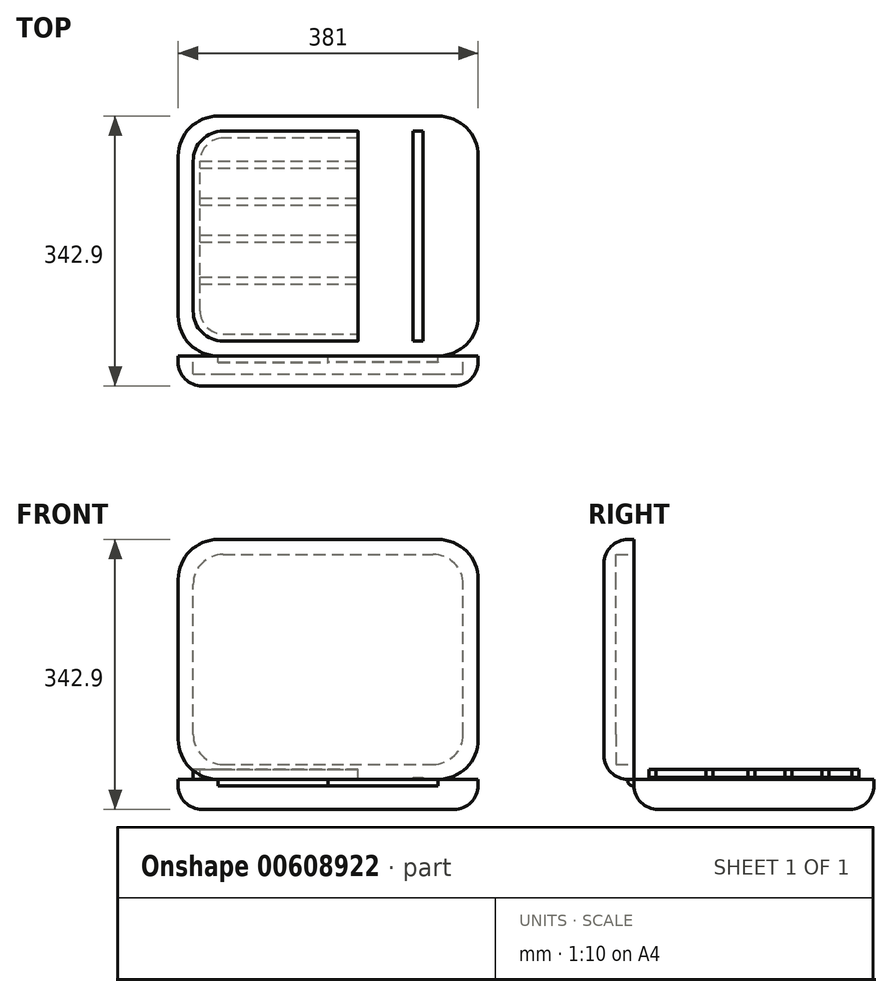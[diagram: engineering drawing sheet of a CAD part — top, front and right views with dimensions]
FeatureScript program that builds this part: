
annotation { "Feature Type Name" : "Feature", "Feature Type Description" : "" }
export const myFeature = defineFeature(function(context is Context, id is Id, definition is map)
    precondition{}
    {
        {
            var Q0;
            Q0=qCreatedBy(makeId("Top.planeOp"),FACE);
            var sketch = newSketch(context, id + "F0", { "sketchPlane" : qUnion([Q0])});
            skLineSegment(sketch, "E0.bottom", {"start": v(139.7, -152.4) * mm, "end": v(-139.7, -152.4) * mm});
            skLineSegment(sketch, "E0.top", {"start": v(139.7, 152.4) * mm, "end": v(-139.7, 152.4) * mm});
            skLineSegment(sketch, "E0.left", {"start": v(190.5, -101.6) * mm, "end": v(190.5, 101.6) * mm});
            skLineSegment(sketch, "E0.right", {"start": v(-190.5, -101.6) * mm, "end": v(-190.5, 101.6) * mm});
            skPoint(sketch, "E0.middle", {"position": v(0, 0) * mm});
            skPoint(sketch, "E1.visualSharp", {"position": v(-190.5, 152.4) * mm});
            skArc(sketch, "E1.filletArc", {"start": v(-139.7, 152.4) * mm, "mid": v(-175.62, 137.52) * mm, "end": v(-190.5, 101.6) * mm});
            skPoint(sketch, "E2.visualSharp", {"position": v(190.5, 152.4) * mm});
            skArc(sketch, "E2.filletArc", {"start": v(190.5, 101.6) * mm, "mid": v(175.62, 137.52) * mm, "end": v(139.7, 152.4) * mm});
            skPoint(sketch, "E3.visualSharp", {"position": v(190.5, -152.4) * mm});
            skArc(sketch, "E3.filletArc", {"start": v(139.7, -152.4) * mm, "mid": v(175.62, -137.52) * mm, "end": v(190.5, -101.6) * mm});
            skPoint(sketch, "E4.visualSharp", {"position": v(-190.5, -152.4) * mm});
            skArc(sketch, "E4.filletArc", {"start": v(-190.5, -101.6) * mm, "mid": v(-175.62, -137.52) * mm, "end": v(-139.7, -152.4) * mm});
            skSolve(sketch);
        }
        {
            var Q0;
            Q0=makeQuery(id+"F0.imprint","IMPRINT",FACE,{"disambiguationData":[TD([[makeQuery(id+"F0.imprint","IMPRINT",EDGE,{"derivedFrom":sQuery(id+"F0.wireOp",EDGE,"E0.bottom")}),-1.0]])]});
            extrude(context, id + "F1", {"entities" : qUnion([Q0]), "depth" : 38.1 * mm, "offsetDistance" : 25.4 * mm});
        }
        {
            var Q0;
            Q0=makeQuery(id+"F1.opExtrude","CAP_EDGE",EDGE,{"disambiguationData":[OSD([sQuery(id+"F0.wireOp",EDGE,"E0.bottom")])],"isStart":true});
            fillet(context, id + "F2", {"entities" : qUnion([Q0]), "radius" : 30.48 * mm, "tangentPropagation" : true, "allowEdgeOverflow" : false});
        }
        {
            var Q0;
            Q0=makeQuery(id+"F1.opExtrude","SWEPT_FACE",FACE,{"disambiguationData":[OSD([sQuery(id+"F0.wireOp",EDGE,"E0.bottom")])]});
            var sketch = newSketch(context, id + "F3", { "sketchPlane" : qUnion([Q0])});
            skLineSegment(sketch, "E5.bottom", {"start": v(-139.7, 342.9) * mm, "end": v(139.7, 342.9) * mm});
            skLineSegment(sketch, "E5.top", {"start": v(-139.7, 38.1) * mm, "end": v(139.7, 38.1) * mm});
            skLineSegment(sketch, "E5.left", {"start": v(-190.5, 292.1) * mm, "end": v(-190.5, 88.9) * mm});
            skLineSegment(sketch, "E5.right", {"start": v(190.5, 292.1) * mm, "end": v(190.5, 88.9) * mm});
            skPoint(sketch, "E6.visualSharp", {"position": v(-190.5, 342.9) * mm});
            skArc(sketch, "E6.filletArc", {"start": v(-139.7, 342.9) * mm, "mid": v(-175.62, 328.02) * mm, "end": v(-190.5, 292.1) * mm});
            skPoint(sketch, "E7.visualSharp", {"position": v(190.5, 342.9) * mm});
            skArc(sketch, "E7.filletArc", {"start": v(190.5, 292.1) * mm, "mid": v(175.62, 328.02) * mm, "end": v(139.7, 342.9) * mm});
            skPoint(sketch, "E8.visualSharp", {"position": v(190.5, 38.1) * mm});
            skArc(sketch, "E8.filletArc", {"start": v(139.7, 38.1) * mm, "mid": v(175.62, 52.98) * mm, "end": v(190.5, 88.9) * mm});
            skPoint(sketch, "E9.visualSharp", {"position": v(-190.5, 38.1) * mm});
            skArc(sketch, "E9.filletArc", {"start": v(-190.5, 88.9) * mm, "mid": v(-175.62, 52.98) * mm, "end": v(-139.7, 38.1) * mm});
            skSolve(sketch);
        }
        {
            var Q0;
            Q0 = qSketchRegion(id + "F3", true);
            extrude(context, id + "F4", {"entities" : qUnion([Q0]), "depth" : 38.1 * mm, "offsetDistance" : 25.4 * mm});
        }
        {
            var Q0;
            Q0=makeQuery(id+"F4.opExtrude","CAP_EDGE",EDGE,{"disambiguationData":[OSD([sQuery(id+"F3.wireOp",EDGE,"E5.left")])],"isStart":false});
            fillet(context, id + "F5", {"entities" : qUnion([Q0]), "radius" : 30.48 * mm, "tangentPropagation" : true, "allowEdgeOverflow" : false});
        }
        {
            var Q0;
            Q0=qCreatedBy(makeId("Right.planeOp"),FACE);
            var sketch = newSketch(context, id + "F6", { "sketchPlane" : qUnion([Q0])});
            skArc(sketch, "E10", {"start": v(-160.02, 38.1) * mm, "mid": v(-158.64, 31.86) * mm, "end": v(-152.4, 30.48) * mm});
            skLineSegment(sketch, "E11", {"start": v(-160.02, 38.1) * mm, "end": v(-152.4, 38.1) * mm});
            skLineSegment(sketch, "E12", {"start": v(-152.4, 38.1) * mm, "end": v(-152.4, 30.48) * mm});
            skSolve(sketch);
        }
        {
            var Q0;
            Q0 = qSketchRegion(id + "F6", true);
            extrude(context, id + "F7", {"entities" : qUnion([Q0]), "depth" : 139.7 * mm, "offsetDistance" : 25.4 * mm});
        }
        {
            var Q0;
            Q0=makeQuery(id+"F7.opExtrude","CAP_FACE",FACE,{"disambiguationData":[OSD([sQuery(id+"F6.wireOp",EDGE,"E10"),sQuery(id+"F6.wireOp",EDGE,"E11"),sQuery(id+"F6.wireOp",EDGE,"E12")])],"isStart":true});
            extrude(context, id + "F8", {"entities" : qUnion([Q0]), "depth" : 139.7 * mm, "offsetDistance" : 25.4 * mm});
        }
        {
            var Q0;
            Q0=makeQuery(id+"F4.opExtrude","CAP_FACE",FACE,{"disambiguationData":[OSD([sQuery(id+"F3.wireOp",EDGE,"E5.bottom"),sQuery(id+"F3.wireOp",EDGE,"E5.top"),sQuery(id+"F3.wireOp",EDGE,"E5.left"),sQuery(id+"F3.wireOp",EDGE,"E5.right"),sQuery(id+"F3.wireOp",EDGE,"E6.filletArc"),sQuery(id+"F3.wireOp",EDGE,"E7.filletArc"),sQuery(id+"F3.wireOp",EDGE,"E8.filletArc"),sQuery(id+"F3.wireOp",EDGE,"E9.filletArc")])],"isStart":true});
            var sketch = newSketch(context, id + "F9", { "sketchPlane" : qUnion([Q0])});
            skLineSegment(sketch, "E13.bottom", {"start": v(133.35, 57.15) * mm, "end": v(-133.35, 57.15) * mm});
            skLineSegment(sketch, "E13.top", {"start": v(133.35, 323.85) * mm, "end": v(-133.35, 323.85) * mm});
            skLineSegment(sketch, "E13.left", {"start": v(171.45, 95.25) * mm, "end": v(171.45, 285.75) * mm});
            skLineSegment(sketch, "E13.right", {"start": v(-171.45, 95.25) * mm, "end": v(-171.45, 285.75) * mm});
            skPoint(sketch, "E13.middle", {"position": v(0, 190.5) * mm});
            skPoint(sketch, "E14.visualSharp", {"position": v(-171.45, 323.85) * mm});
            skArc(sketch, "E14.filletArc", {"start": v(-133.35, 323.85) * mm, "mid": v(-160.3, 312.7) * mm, "end": v(-171.45, 285.75) * mm});
            skPoint(sketch, "E15.visualSharp", {"position": v(171.45, 323.85) * mm});
            skArc(sketch, "E15.filletArc", {"start": v(171.45, 285.75) * mm, "mid": v(160.3, 312.7) * mm, "end": v(133.35, 323.85) * mm});
            skPoint(sketch, "E16.visualSharp", {"position": v(171.45, 57.15) * mm});
            skArc(sketch, "E16.filletArc", {"start": v(133.35, 57.15) * mm, "mid": v(160.3, 68.3) * mm, "end": v(171.45, 95.25) * mm});
            skPoint(sketch, "E17.visualSharp", {"position": v(-171.45, 57.15) * mm});
            skArc(sketch, "E17.filletArc", {"start": v(-171.45, 95.25) * mm, "mid": v(-160.3, 68.3) * mm, "end": v(-133.35, 57.15) * mm});
            skSolve(sketch);
        }
        {
            var Q0;
            Q0 = qSketchRegion(id + "F9", true);
            extrude(context, id + "F10", {"entities" : qUnion([Q0]), "operationType" : NewBodyOperationType.REMOVE, "oppositeDirection" : true, "depth" : 22.86 * mm, "offsetDistance" : 25.4 * mm});
        }
        {
            var Q0;
            Q0=makeQuery(id+"F1.opExtrude","CAP_FACE",FACE,{"disambiguationData":[OSD([sQuery(id+"F0.wireOp",EDGE,"E0.bottom"),sQuery(id+"F0.wireOp",EDGE,"E0.top"),sQuery(id+"F0.wireOp",EDGE,"E0.left"),sQuery(id+"F0.wireOp",EDGE,"E0.right"),sQuery(id+"F0.wireOp",EDGE,"E1.filletArc"),sQuery(id+"F0.wireOp",EDGE,"E2.filletArc"),sQuery(id+"F0.wireOp",EDGE,"E3.filletArc"),sQuery(id+"F0.wireOp",EDGE,"E4.filletArc")])],"isStart":false});
            var sketch = newSketch(context, id + "F11", { "sketchPlane" : qUnion([Q0])});
            skSolve(sketch);
        }
        {
            var Q0;
            Q0=makeQuery(id+"F11.imprint","IMPRINT",FACE,{"disambiguationData":[TD([[makeQuery(id+"F11.imprint","IMPRINT",EDGE,{"derivedFrom":makeQuery(id+"F1.opExtrude","CAP_EDGE",EDGE,{"disambiguationData":[OSD([sQuery(id+"F0.wireOp",EDGE,"E0.bottom")])],"isStart":false})}),-1.0]])]});
            var sketch = newSketch(context, id + "F12", { "sketchPlane" : qUnion([Q0])});
            skLineSegment(sketch, "E18.bottom", {"start": v(-133.35, 133.35) * mm, "end": v(38.1, 133.35) * mm});
            skLineSegment(sketch, "E18.top", {"start": v(-133.35, -133.35) * mm, "end": v(38.1, -133.35) * mm});
            skLineSegment(sketch, "E18.left", {"start": v(-171.45, 95.25) * mm, "end": v(-171.45, -95.25) * mm});
            skLineSegment(sketch, "E19", {"start": v(190.5, 0) * mm, "end": v(171.45, 0) * mm});
            skPoint(sketch, "E20.visualSharp", {"position": v(-171.45, 133.35) * mm});
            skArc(sketch, "E20.filletArc", {"start": v(-133.35, 133.35) * mm, "mid": v(-160.3, 122.2) * mm, "end": v(-171.45, 95.25) * mm});
            skPoint(sketch, "E21.visualSharp", {"position": v(-171.45, -133.35) * mm});
            skArc(sketch, "E21.filletArc", {"start": v(-171.45, -95.25) * mm, "mid": v(-160.3, -122.2) * mm, "end": v(-133.35, -133.35) * mm});
            skLineSegment(sketch, "E22", {"start": v(38.1, 133.35) * mm, "end": v(38.1, 124.46) * mm});
            skLineSegment(sketch, "E23", {"start": v(38.1, 124.46) * mm, "end": v(-133.35, 124.46) * mm});
            skLineSegment(sketch, "E24", {"start": v(-133.35, -124.46) * mm, "end": v(38.1, -124.46) * mm});
            skArc(sketch, "E25", {"start": v(-162.56, -95.25) * mm, "mid": v(-154, -115.9) * mm, "end": v(-133.35, -124.46) * mm});
            skLineSegment(sketch, "E26", {"start": v(38.1, -124.46) * mm, "end": v(38.1, -133.35) * mm});
            skLineSegment(sketch, "E27", {"start": v(-162.56, -95.25) * mm, "end": v(-162.56, 95.25) * mm});
            skArc(sketch, "E28", {"start": v(-133.35, 124.46) * mm, "mid": v(-154, 115.9) * mm, "end": v(-162.56, 95.25) * mm});
            skSolve(sketch);
        }
        {
            var Q0;
            Q0 = qSketchRegion(id + "F12", true);
            extrude(context, id + "F13", {"entities" : qUnion([Q0]), "depth" : 12.7 * mm, "offsetDistance" : 25.4 * mm});
        }
        {
            var Q0;
            Q0=makeQuery(id+"F13.opExtrude","CAP_FACE",FACE,{"disambiguationData":[OSD([sQuery(id+"F12.wireOp",EDGE,"E18.bottom"),sQuery(id+"F12.wireOp",EDGE,"E18.top"),sQuery(id+"F12.wireOp",EDGE,"E18.left"),sQuery(id+"F12.wireOp",EDGE,"E20.filletArc"),sQuery(id+"F12.wireOp",EDGE,"E21.filletArc"),sQuery(id+"F12.wireOp",EDGE,"E23"),sQuery(id+"F12.wireOp",EDGE,"E24"),sQuery(id+"F12.wireOp",EDGE,"E25"),sQuery(id+"F12.wireOp",EDGE,"E22"),sQuery(id+"F12.wireOp",EDGE,"E26"),sQuery(id+"F12.wireOp",EDGE,"E27"),sQuery(id+"F12.wireOp",EDGE,"E28")])],"isStart":false});
            var sketch = newSketch(context, id + "F14", { "sketchPlane" : qUnion([Q0])});
            skLineSegment(sketch, "E29.bottom", {"start": v(-162.56, 95.25) * mm, "end": v(38.1, 95.25) * mm});
            skLineSegment(sketch, "E29.top", {"start": v(-162.56, 86.36) * mm, "end": v(38.1, 86.36) * mm});
            skLineSegment(sketch, "E29.left", {"start": v(-162.56, 95.25) * mm, "end": v(-162.56, 86.36) * mm});
            skLineSegment(sketch, "E29.right", {"start": v(38.1, 95.25) * mm, "end": v(38.1, 86.36) * mm});
            skLineSegment(sketch, "E30.bottom", {"start": v(-162.56, 48.26) * mm, "end": v(38.1, 48.26) * mm});
            skLineSegment(sketch, "E30.top", {"start": v(-162.56, 39.37) * mm, "end": v(38.1, 39.37) * mm});
            skLineSegment(sketch, "E30.left", {"start": v(-162.56, 48.26) * mm, "end": v(-162.56, 39.37) * mm});
            skLineSegment(sketch, "E30.right", {"start": v(38.1, 48.26) * mm, "end": v(38.1, 39.37) * mm});
            skLineSegment(sketch, "E31.bottom", {"start": v(-162.56, 1.27) * mm, "end": v(38.1, 1.27) * mm});
            skLineSegment(sketch, "E31.top", {"start": v(-162.56, -7.62) * mm, "end": v(38.1, -7.62) * mm});
            skLineSegment(sketch, "E31.left", {"start": v(-162.56, 1.27) * mm, "end": v(-162.56, -7.62) * mm});
            skLineSegment(sketch, "E31.right", {"start": v(38.1, 1.27) * mm, "end": v(38.1, -7.62) * mm});
            skLineSegment(sketch, "E32.bottom", {"start": v(-162.56, -52.07) * mm, "end": v(38.1, -52.07) * mm});
            skLineSegment(sketch, "E32.top", {"start": v(-162.56, -60.96) * mm, "end": v(38.1, -60.96) * mm});
            skLineSegment(sketch, "E32.left", {"start": v(-162.56, -52.07) * mm, "end": v(-162.56, -60.96) * mm});
            skLineSegment(sketch, "E32.right", {"start": v(38.1, -52.07) * mm, "end": v(38.1, -60.96) * mm});
            skSolve(sketch);
        }
        {
            var Q0;
            Q0 = qSketchRegion(id + "F14", true);
            extrude(context, id + "F15", {"entities" : qUnion([Q0]), "oppositeDirection" : true, "depth" : 12.7 * mm, "offsetDistance" : 25.4 * mm});
        }
        {
            var Q0;
            Q0=makeQuery(id+"F13.opExtrude","CAP_FACE",FACE,{"disambiguationData":[OSD([sQuery(id+"F12.wireOp",EDGE,"E18.bottom"),sQuery(id+"F12.wireOp",EDGE,"E18.top"),sQuery(id+"F12.wireOp",EDGE,"E18.left"),sQuery(id+"F12.wireOp",EDGE,"E20.filletArc"),sQuery(id+"F12.wireOp",EDGE,"E21.filletArc"),sQuery(id+"F12.wireOp",EDGE,"E23"),sQuery(id+"F12.wireOp",EDGE,"E24"),sQuery(id+"F12.wireOp",EDGE,"E25"),sQuery(id+"F12.wireOp",EDGE,"E22"),sQuery(id+"F12.wireOp",EDGE,"E26"),sQuery(id+"F12.wireOp",EDGE,"E27"),sQuery(id+"F12.wireOp",EDGE,"E28")])],"isStart":false});
            var sketch = newSketch(context, id + "F16", { "sketchPlane" : qUnion([Q0])});
            skLineSegment(sketch, "E33.bottom", {"start": v(38.1, 133.35) * mm, "end": v(-133.35, 133.35) * mm});
            skLineSegment(sketch, "E33.top", {"start": v(38.1, -133.35) * mm, "end": v(-133.35, -133.35) * mm});
            skLineSegment(sketch, "E33.left", {"start": v(38.1, 133.35) * mm, "end": v(38.1, -133.35) * mm});
            skLineSegment(sketch, "E33.right", {"start": v(-171.45, 95.25) * mm, "end": v(-171.45, -95.25) * mm});
            skPoint(sketch, "E34.visualSharp", {"position": v(-171.45, 133.35) * mm});
            skArc(sketch, "E34.filletArc", {"start": v(-133.35, 133.35) * mm, "mid": v(-160.3, 122.2) * mm, "end": v(-171.45, 95.25) * mm});
            skPoint(sketch, "E35.visualSharp", {"position": v(-171.45, -133.35) * mm});
            skArc(sketch, "E35.filletArc", {"start": v(-171.45, -95.25) * mm, "mid": v(-160.3, -122.2) * mm, "end": v(-133.35, -133.35) * mm});
            skSolve(sketch);
        }
        {
            var Q0;
            Q0 = qSketchRegion(id + "F16", true);
            extrude(context, id + "F17", {"entities" : qUnion([Q0]), "depth" : 1 / 203.2 * mm, "offsetDistance" : 25.4 * mm});
        }
        {
            var Q0;
            Q0=makeQuery(id+"F17.opExtrude","CAP_EDGE",EDGE,{"disambiguationData":[OSD([sQuery(id+"F16.wireOp",EDGE,"E33.right")])],"isStart":false});
            fillet(context, id + "F18", {"entities" : qUnion([Q0]), "radius" : 6.35 * mm, "tangentPropagation" : true, "allowEdgeOverflow" : false});
        }
        {
            var Q0;
            Q0=makeQuery(id+"F11.imprint","IMPRINT",FACE,{"disambiguationData":[TD([[makeQuery(id+"F11.imprint","IMPRINT",EDGE,{"derivedFrom":makeQuery(id+"F1.opExtrude","CAP_EDGE",EDGE,{"disambiguationData":[OSD([sQuery(id+"F0.wireOp",EDGE,"E0.bottom")])],"isStart":false})}),-1.0]])]});
            var sketch = newSketch(context, id + "F19", { "sketchPlane" : qUnion([Q0])});
            skLineSegment(sketch, "E36.bottom", {"start": v(107.95, 133.35) * mm, "end": v(120.65, 133.35) * mm});
            skLineSegment(sketch, "E36.top", {"start": v(107.95, -133.35) * mm, "end": v(120.65, -133.35) * mm});
            skLineSegment(sketch, "E36.left", {"start": v(107.95, 133.35) * mm, "end": v(107.95, -133.35) * mm});
            skLineSegment(sketch, "E36.right", {"start": v(120.65, 133.35) * mm, "end": v(120.65, -133.35) * mm});
            skSolve(sketch);
        }
        {
            var Q0;
            Q0 = qSketchRegion(id + "F19", true);
            extrude(context, id + "F20", {"entities" : qUnion([Q0]), "depth" : 2.54 * mm, "offsetDistance" : 25.4 * mm});
        }
    });
